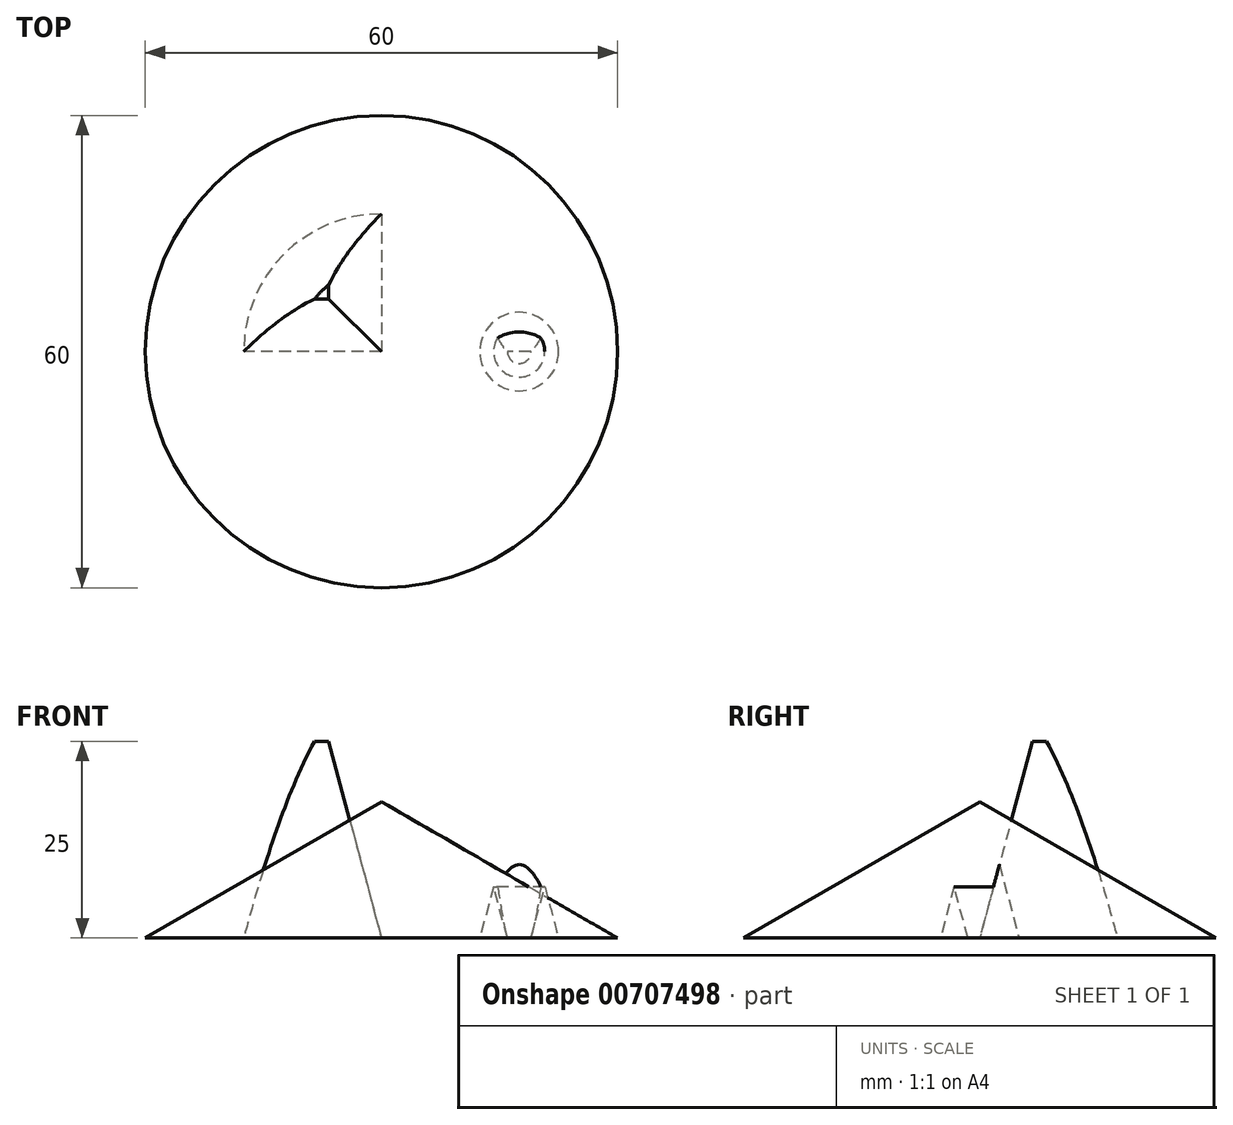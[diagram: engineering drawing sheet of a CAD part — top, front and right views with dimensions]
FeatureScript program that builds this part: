
annotation { "Feature Type Name" : "Feature", "Feature Type Description" : "" }
export const myFeature = defineFeature(function(context is Context, id is Id, definition is map)
    precondition{}
    {
        {
            var Q0;
            Q0=qCreatedBy(makeId("Top.planeOp"),FACE);
            var sketch = newSketch(context, id + "F0", { "sketchPlane" : qUnion([Q0])});
            skCircle(sketch, "E0", {"center": v(0, 0) * mm, "radius": 30 * mm});
            skSolve(sketch);
        }
        {
            var Q0;
            Q0=makeQuery(id+"F0.imprint","IMPRINT",FACE,{"disambiguationData":[TD([[makeQuery(id+"F0.imprint","IMPRINT",EDGE,{"derivedFrom":sQuery(id+"F0.wireOp",EDGE,"E0")}),1.0]])]});
            extrude(context, id + "F1", {"entities" : qUnion([Q0]), "depth" : 30 * mm, "hasOffset" : true, "offsetDistance" : 25 * mm, "hasDraft" : true, "draftAngle" : 60 * degree, "draftPullDirection" : true});
        }
        {
            var Q0;
            Q0=qCreatedBy(makeId("Top.planeOp"),FACE);
            var sketch = newSketch(context, id + "F2", { "sketchPlane" : qUnion([Q0])});
            skCircle(sketch, "E1", {"center": v(0, 0) * mm, "radius": 17.5 * mm});
            skLineSegment(sketch, "E2", {"start": v(0, 23.44) * mm, "end": v(0, -21.3) * mm});
            skLineSegment(sketch, "E3", {"start": v(21.02, 0) * mm, "end": v(-21.55, 0) * mm});
            skCircle(sketch, "E4", {"center": v(17.5, 0) * mm, "radius": 5 * mm});
            skCircle(sketch, "E5", {"center": v(17.5, 0) * mm, "radius": 1.5 * mm});
            skSolve(sketch);
        }
        {
            var Q0;
            {var subQ2=sQuery(id+"F2.wireOp",EDGE,"E1");var subQ4=sQuery(id+"F2.wireOp",EDGE,"E4");var subQ5=makeQuery(id+"F2.imprint","INTERSECT",VERTEX,{"disambiguationData":[OD(0.0)],"derivedFrom":[subQ2,subQ4]});Q0=makeQuery(id+"F2.imprint","IMPRINT",FACE,{"disambiguationData":[TD([[makeQuery(id+"F2.imprint","IMPRINT",EDGE,{"disambiguationData":[TD([[subQ5,1.0]])],"derivedFrom":subQ2}),-1.0]])]});}
            var Q1;
            {var subQ0=sQuery(id+"F2.wireOp",EDGE,"E4");var subQ1=sQuery(id+"F2.wireOp",EDGE,"E1");var subQ2=makeQuery(id+"F2.imprint","INTERSECT",VERTEX,{"disambiguationData":[OD(0.0)],"derivedFrom":[subQ1,subQ0]});Q1=makeQuery(id+"F2.imprint","IMPRINT",FACE,{"disambiguationData":[TD([[makeQuery(id+"F2.imprint","IMPRINT",EDGE,{"disambiguationData":[TD([[subQ2,1.0]])],"derivedFrom":subQ1}),1.0]])]});}
            var Q2;
            {var subQ0=sQuery(id+"F2.wireOp",EDGE,"E5");var subQ1=sQuery(id+"F2.wireOp",EDGE,"E1");var subQ2=makeQuery(id+"F2.imprint","INTERSECT",VERTEX,{"disambiguationData":[OD(0.0)],"derivedFrom":[subQ1,subQ0]});Q2=makeQuery(id+"F2.imprint","IMPRINT",FACE,{"disambiguationData":[TD([[makeQuery(id+"F2.imprint","IMPRINT",EDGE,{"disambiguationData":[TD([[subQ2,1.0]])],"derivedFrom":subQ1}),-1.0]])]});}
            var Q3;
            {var subQ0=sQuery(id+"F2.wireOp",EDGE,"E5");var subQ1=sQuery(id+"F2.wireOp",EDGE,"E1");var subQ2=makeQuery(id+"F2.imprint","INTERSECT",VERTEX,{"disambiguationData":[OD(0.0)],"derivedFrom":[subQ1,subQ0]});Q3=makeQuery(id+"F2.imprint","IMPRINT",FACE,{"disambiguationData":[TD([[makeQuery(id+"F2.imprint","IMPRINT",EDGE,{"disambiguationData":[TD([[subQ2,1.0]])],"derivedFrom":subQ1}),1.0]])]});}
            var Q4;
            {var subQ0=sQuery(id+"F2.wireOp",EDGE,"E3");var subQ1=sQuery(id+"F2.wireOp",EDGE,"E1");var subQ2=makeQuery(id+"F2.imprint","INTERSECT",VERTEX,{"disambiguationData":[OD(1.0)],"derivedFrom":[subQ1,subQ0]});Q4=makeQuery(id+"F2.imprint","IMPRINT",FACE,{"disambiguationData":[TD([[makeQuery(id+"F2.imprint","IMPRINT",EDGE,{"disambiguationData":[TD([[subQ2,1.0]])],"derivedFrom":subQ1}),-1.0]])]});}
            var Q5;
            {var subQ0=sQuery(id+"F2.wireOp",EDGE,"E3");var subQ1=sQuery(id+"F2.wireOp",EDGE,"E1");var subQ2=makeQuery(id+"F2.imprint","INTERSECT",VERTEX,{"disambiguationData":[OD(1.0)],"derivedFrom":[subQ1,subQ0]});Q5=makeQuery(id+"F2.imprint","IMPRINT",FACE,{"disambiguationData":[TD([[makeQuery(id+"F2.imprint","IMPRINT",EDGE,{"disambiguationData":[TD([[subQ2,1.0]])],"derivedFrom":subQ1}),1.0]])]});}
            var Q6;
            {var subQ0=sQuery(id+"F2.wireOp",EDGE,"E4");var subQ1=sQuery(id+"F2.wireOp",EDGE,"E1");var subQ2=makeQuery(id+"F2.imprint","INTERSECT",VERTEX,{"disambiguationData":[OD(1.0)],"derivedFrom":[subQ1,subQ0]});Q6=makeQuery(id+"F2.imprint","IMPRINT",FACE,{"disambiguationData":[TD([[makeQuery(id+"F2.imprint","IMPRINT",EDGE,{"disambiguationData":[TD([[subQ2,-1.0]])],"derivedFrom":subQ1}),1.0]])]});}
            extrude(context, id + "F3", {"entities" : qUnion([Q0, Q1, Q2, Q3, Q4, Q5, Q6]), "depth" : 25 * mm, "offsetDistance" : 25 * mm, "hasDraft" : true, "draftAngle" : 15 * degree, "draftPullDirection" : true});
        }
    });
